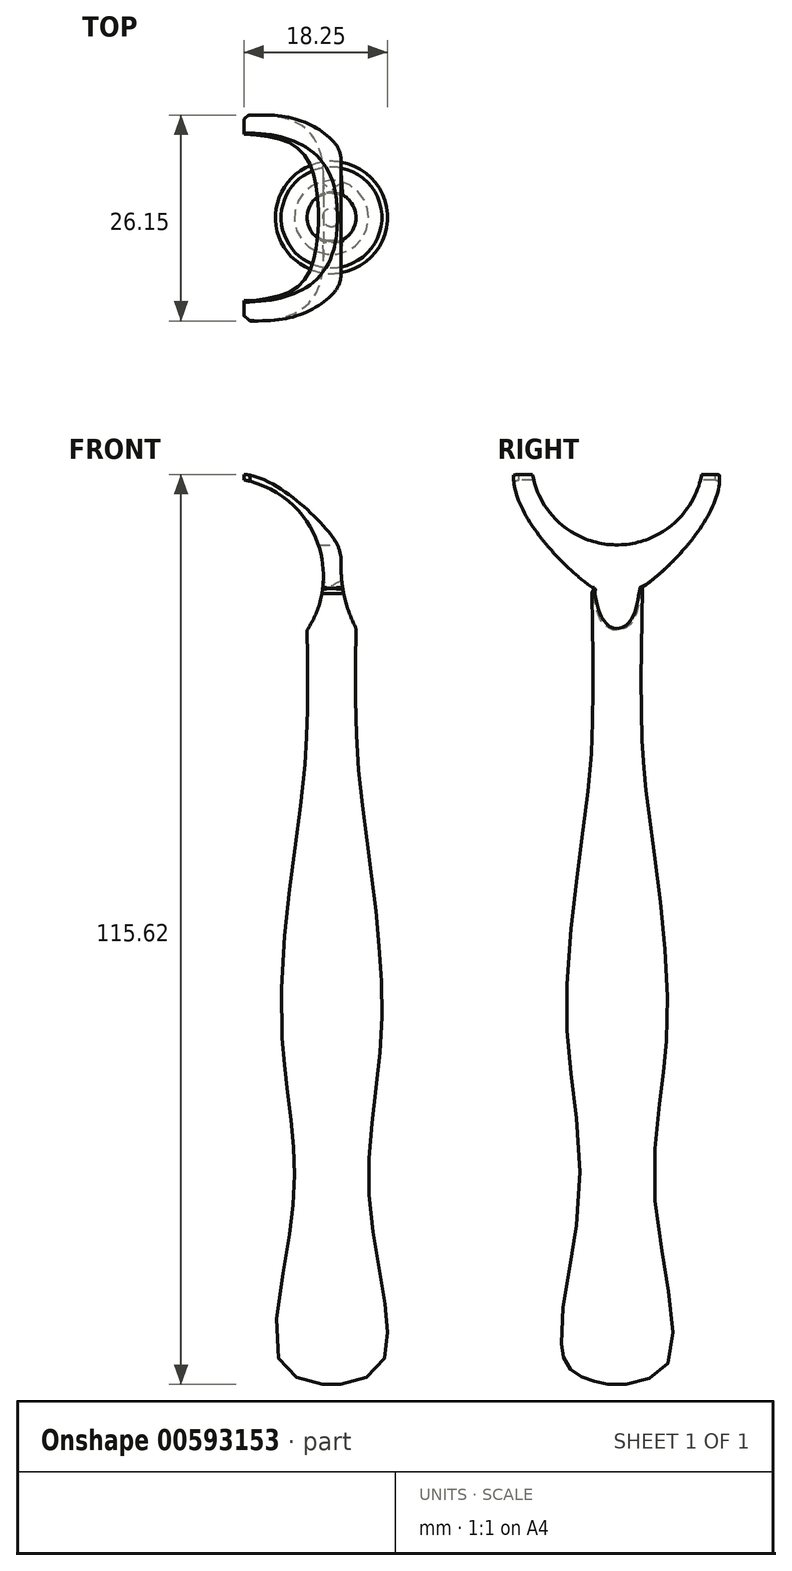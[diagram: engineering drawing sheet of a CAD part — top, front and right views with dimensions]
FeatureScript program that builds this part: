
annotation { "Feature Type Name" : "Feature", "Feature Type Description" : "" }
export const myFeature = defineFeature(function(context is Context, id is Id, definition is map)
    precondition{}
    {
        {
            var Q0;
            Q0=qCreatedBy(makeId("Front.planeOp"),FACE);
            var sketch = newSketch(context, id + "F0", { "sketchPlane" : qUnion([Q0])});
            skLineSegment(sketch, "E0", {"start": v(0, 66.8) * mm, "end": v(-16.72, 66.8) * mm});
            skLineSegment(sketch, "E1", {"start": v(-16.72, 66.8) * mm, "end": v(-16.72, 52.2) * mm});
            skLineSegment(sketch, "E2", {"start": v(-16.72, 52.2) * mm, "end": v(-3.2, 52.2) * mm});
            skFitSpline(sketch, "E3", {"points": [v(-3.2, 52.2) * mm, v(-3.2, 32.41) * mm, v(-4.57, 19.45) * mm, v(-6.35, -3.89) * mm, v(-4.85, -25.86) * mm, v(-6.62, -46.06) * mm, v(-1.16, -49.07) * mm], "startDerivative": vector(2.22, -117.74) * mm, "endDerivative": vector(67.26, -13.91) * mm});
            skLineSegment(sketch, "E4", {"start": v(0, 66.8) * mm, "end": v(0, -49.07) * mm});
            skLineSegment(sketch, "E5", {"start": v(0, -49.07) * mm, "end": v(-1.16, -49.07) * mm});
            skSolve(sketch);
        }
        {
            var Q0;
            Q0=makeQuery(id+"F0.imprint","IMPRINT",FACE,{"disambiguationData":[TD([[makeQuery(id+"F0.imprint","IMPRINT",EDGE,{"derivedFrom":sQuery(id+"F0.wireOp",EDGE,"E0")}),1.0]])]});
            var Q1;
            Q1=sQuery(id+"F0.wireOp",EDGE,"E4");
            revolve(context, id + "F1", {"entities" : qUnion([Q0]), "axis" : qUnion([Q1]), "revolveType" : RevolveType.FULL});
        }
        {
            var Q0;
            Q0=qCreatedBy(makeId("Front.planeOp"),FACE);
            var sketch = newSketch(context, id + "F2", { "sketchPlane" : qUnion([Q0])});
            skFitSpline(sketch, "E6", {"points": [v(-3.17, 52.2) * mm, v(-2.9, 58.06) * mm, v(-7.07, 63.47) * mm, v(-11.12, 65.84) * mm], "startDerivative": vector(6.27, 21.79) * mm, "endDerivative": vector(-13.93, 5.63) * mm});
            skLineSegment(sketch, "E7", {"start": v(-11.12, 65.84) * mm, "end": v(-11.12, 66.55) * mm});
            skFitSpline(sketch, "E8", {"points": [v(-11.12, 66.55) * mm, v(-3.96, 62.82) * mm, v(3.2, 52.16) * mm], "startDerivative": vector(15.93, -1.08) * mm, "endDerivative": vector(7.9, -27.96) * mm});
            skLineSegment(sketch, "E9", {"start": v(3.2, 52.16) * mm, "end": v(4.47, 49.72) * mm});
            skLineSegment(sketch, "E10", {"start": v(4.47, 49.72) * mm, "end": v(19.86, 52.16) * mm});
            skLineSegment(sketch, "E11", {"start": v(19.86, 52.16) * mm, "end": v(18.2, 69.8) * mm});
            skLineSegment(sketch, "E12", {"start": v(18.2, 69.8) * mm, "end": v(-2.21, 71.42) * mm});
            skLineSegment(sketch, "E13", {"start": v(-2.21, 71.42) * mm, "end": v(-21.01, 66.4) * mm});
            skLineSegment(sketch, "E14", {"start": v(-21.01, 66.4) * mm, "end": v(-18.9, 49.16) * mm});
            skLineSegment(sketch, "E15", {"start": v(-18.9, 49.16) * mm, "end": v(-3.17, 52.2) * mm});
            skSolve(sketch);
        }
        {
            var Q0;
            Q0 = qSketchRegion(id + "F2", true);
            var Q1;
            Q1=makeQuery(id+"F2.imprint","IMPRINT",FACE,{"disambiguationData":[TD([[makeQuery(id+"F2.imprint","IMPRINT",EDGE,{"derivedFrom":sQuery(id+"F2.wireOp",EDGE,"E6")}),1.0]])]});
            extrude(context, id + "F3", {"entities" : qUnion([Q0, Q1]), "operationType" : NewBodyOperationType.REMOVE, "endBound" : BoundingType.SYMMETRIC, "oppositeDirection" : true, "depth" : 64.2 * mm, "offsetDistance" : 25 * mm});
        }
        {
            var Q0;
            Q0=qCreatedBy(makeId("Right.planeOp"),FACE);
            var sketch = newSketch(context, id + "F4", { "sketchPlane" : qUnion([Q0])});
            skCircle(sketch, "E16", {"center": v(0, 68.51) * mm, "radius": 10.92 * mm});
            skSolve(sketch);
        }
        {
            var Q0;
            Q0 = qSketchRegion(id + "F4", true);
            var Q1;
            Q1=makeQuery(id+"F4.imprint","IMPRINT",FACE,{"disambiguationData":[TD([[makeQuery(id+"F4.imprint","IMPRINT",EDGE,{"derivedFrom":sQuery(id+"F4.wireOp",EDGE,"E16")}),1.0]])]});
            extrude(context, id + "F5", {"entities" : qUnion([Q0, Q1]), "operationType" : NewBodyOperationType.REMOVE, "endBound" : BoundingType.SYMMETRIC, "oppositeDirection" : true, "depth" : 25 * mm, "offsetDistance" : 25 * mm});
        }
        {
            var Q0;
            Q0=qCreatedBy(makeId("Front.planeOp"),FACE);
            var sketch = newSketch(context, id + "F6", { "sketchPlane" : qUnion([Q0])});
            skCircle(sketch, "E17", {"center": v(-13.45, 53.63) * mm, "radius": 12.43 * mm});
            skSolve(sketch);
        }
        {
            var Q0;
            Q0 = qSketchRegion(id + "F6", true);
            var Q1;
            Q1=makeQuery(id+"F6.imprint","IMPRINT",FACE,{"disambiguationData":[TD([[makeQuery(id+"F6.imprint","IMPRINT",EDGE,{"derivedFrom":sQuery(id+"F6.wireOp",EDGE,"E17")}),1.0]])]});
            extrude(context, id + "F7", {"entities" : qUnion([Q0, Q1]), "operationType" : NewBodyOperationType.REMOVE, "endBound" : BoundingType.SYMMETRIC, "oppositeDirection" : true, "depth" : 48.8 * mm, "offsetDistance" : 25 * mm});
        }
        {
            var Q0;
            Q0=qCreatedBy(makeId("Front.planeOp"),FACE);
            var sketch = newSketch(context, id + "F8", { "sketchPlane" : qUnion([Q0])});
            skCircle(sketch, "E18", {"center": v(18.44, 54.84) * mm, "radius": 17.23 * mm});
            skSolve(sketch);
        }
        {
            var Q0;
            Q0 = qSketchRegion(id + "F8", true);
            extrude(context, id + "F9", {"entities" : qUnion([Q0]), "operationType" : NewBodyOperationType.REMOVE, "endBound" : BoundingType.SYMMETRIC, "depth" : 64 * mm, "offsetDistance" : 25 * mm});
        }
        {
            var Q0;
            Q0=makeQuery(id+"F9.boolean.opBoolean","INTERSECT",EDGE,{"derivedFrom":[makeQuery(id+"F3.boolean.opBoolean","COPY",FACE,{"derivedFrom":makeQuery(id+"F3.opExtrude","SWEPT_FACE",FACE,{"disambiguationData":[OSD([sQuery(id+"F2.wireOp",EDGE,"E8")])]})}),makeQuery(id+"F9.opExtrude","SWEPT_FACE",FACE,{"disambiguationData":[OSD([sQuery(id+"F8.wireOp",EDGE,"E18")])]})]});
            fillet(context, id + "F10", {"entities" : qUnion([Q0]), "radius" : 5 * mm, "tangentPropagation" : true, "allowEdgeOverflow" : false});
        }
        {
            var Q0;
            Q0=qCreatedBy(makeId("Right.planeOp"),FACE);
            var sketch = newSketch(context, id + "F11", { "sketchPlane" : qUnion([Q0])});
            skFitSpline(sketch, "E19", {"points": [v(-13.12, 66.68) * mm, v(-2.94, 52.07) * mm, v(3.14, 52.15) * mm, v(12.99, 66.43) * mm, v(0, 73.33) * mm, v(-13.12, 66.68) * mm]});
            skFitSpline(sketch, "E20", {"points": [v(-16.15, 72.75) * mm, v(-24.77, 49.03) * mm, v(-2.94, 52.07) * mm], "startDerivative": vector(-32.67, -59.39) * mm, "endDerivative": vector(60.15, 18.9) * mm});
            skFitSpline(sketch, "E21", {"points": [v(-16.15, 72.75) * mm, v(-13.12, 66.68) * mm], "startDerivative": vector(3.04, -6.08) * mm, "endDerivative": vector(3.04, -6.08) * mm});
            skLineSegment(sketch, "E22", {"start": v(12.99, 66.43) * mm, "end": v(12.99, 69.39) * mm});
            skLineSegment(sketch, "E23", {"start": v(12.99, 69.39) * mm, "end": v(20.7, 68.11) * mm});
            skLineSegment(sketch, "E24", {"start": v(20.7, 68.11) * mm, "end": v(26.71, 48.34) * mm});
            skLineSegment(sketch, "E25", {"start": v(26.71, 48.34) * mm, "end": v(6.23, 49.5) * mm});
            skLineSegment(sketch, "E26", {"start": v(6.23, 49.5) * mm, "end": v(3.14, 52.15) * mm});
            skSolve(sketch);
        }
        {
            var Q0;
            {var subQ0=sQuery(id+"F11.wireOp",EDGE,"E20");Q0=makeQuery(id+"F11.imprint","IMPRINT",FACE,{"disambiguationData":[TD([[makeQuery(id+"F11.imprint","IMPRINT",EDGE,{"derivedFrom":subQ0}),1.0]])]});}
            var Q1;
            {var subQ0=sQuery(id+"F11.wireOp",EDGE,"E22");Q1=makeQuery(id+"F11.imprint","IMPRINT",FACE,{"disambiguationData":[TD([[makeQuery(id+"F11.imprint","IMPRINT",EDGE,{"derivedFrom":subQ0}),-1.0]])]});}
            extrude(context, id + "F12", {"entities" : qUnion([Q0, Q1]), "operationType" : NewBodyOperationType.REMOVE, "endBound" : BoundingType.SYMMETRIC, "oppositeDirection" : true, "depth" : 25 * mm, "offsetDistance" : 25 * mm});
        }
        {
            var Q0;
            Q0=makeQuery(id+"F12.boolean.opBoolean","INTERSECT",EDGE,{"derivedFrom":[makeQuery(id+"F1.opRevolve","SWEPT_FACE",FACE,{"disambiguationData":[OSD([sQuery(id+"F0.wireOp",EDGE,"E3")])]}),makeQuery(id+"F12.opExtrude","SWEPT_FACE",FACE,{"disambiguationData":[OSD([sQuery(id+"F11.wireOp",EDGE,"E20")])]})]});
            fillet(context, id + "F13", {"entities" : qUnion([Q0]), "radius" : 0.8 * mm, "tangentPropagation" : true, "allowEdgeOverflow" : false});
        }
        {
            var Q0;
            {var subQ0=sQuery(id+"F11.wireOp",EDGE,"E19");Q0=makeQuery(id+"F12.boolean.opBoolean","INTERSECT",EDGE,{"derivedFrom":[makeQuery(id+"F3.boolean.opBoolean","SPLIT",FACE,{"disambiguationData":[OD(1.0)],"derivedFrom":makeQuery(id+"F1.opRevolve","SWEPT_FACE",FACE,{"disambiguationData":[OSD([sQuery(id+"F0.wireOp",EDGE,"E2")])]})}),makeQuery(id+"F12.opExtrude","SWEPT_FACE",FACE,{"disambiguationData":[OSD([subQ0]),TDD([makeQuery(id+"F11.imprint","IMPRINT",EDGE,{"disambiguationData":[TD([[makeQuery(id+"F11.imprint","INTERSECT",VERTEX,{"derivedFrom":[subQ0,sQuery(id+"F11.wireOp",EDGE,"E22")]}),1.0]])],"derivedFrom":subQ0})])]})]});}
            fillet(context, id + "F14", {"entities" : qUnion([Q0]), "radius" : 4.5 * mm, "tangentPropagation" : true, "allowEdgeOverflow" : false});
        }
    });
